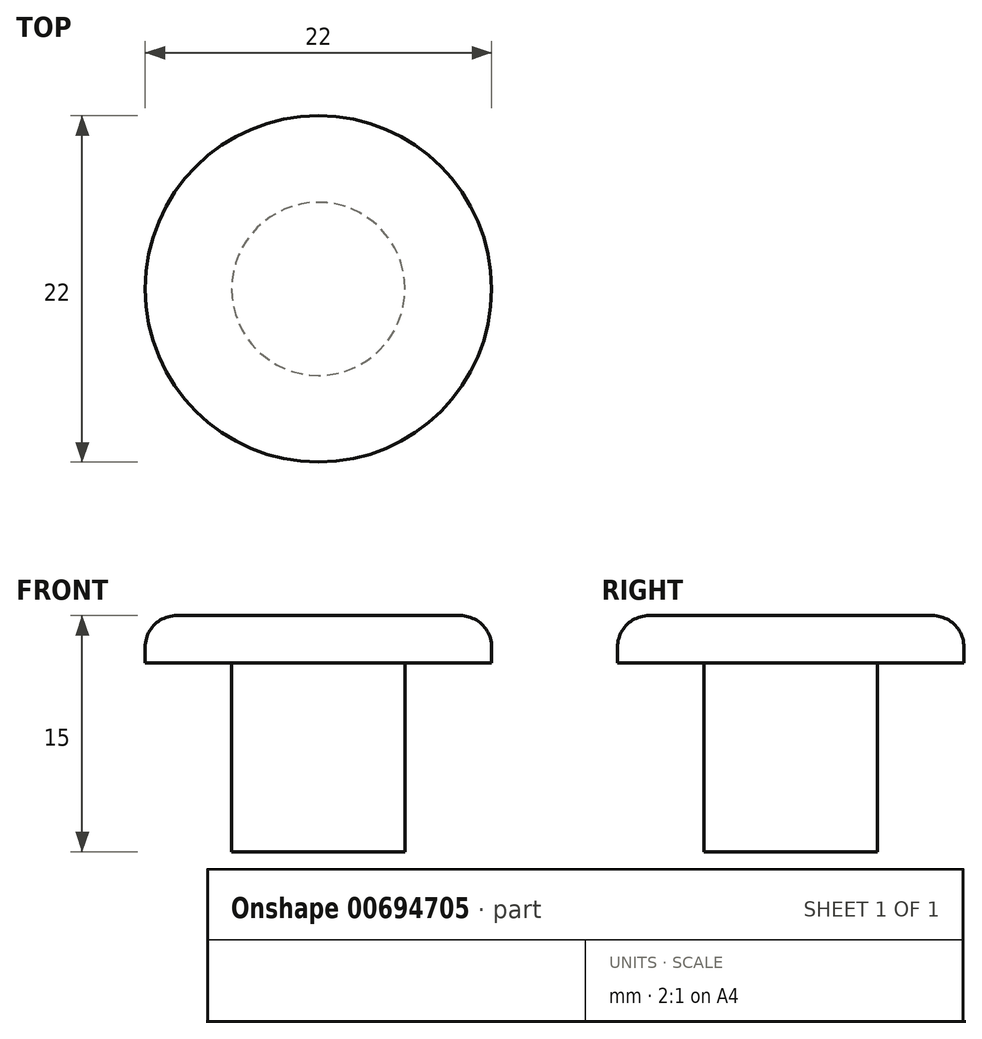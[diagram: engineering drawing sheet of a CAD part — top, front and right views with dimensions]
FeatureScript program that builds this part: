
annotation { "Feature Type Name" : "Feature", "Feature Type Description" : "" }
export const myFeature = defineFeature(function(context is Context, id is Id, definition is map)
    precondition{}
    {
        {
            var Q0;
            Q0=qCreatedBy(makeId("Top.planeOp"),FACE);
            var sketch = newSketch(context, id + "F0", { "sketchPlane" : qUnion([Q0])});
            skCircle(sketch, "E0", {"center": v(0, 0) * mm, "radius": 5.5 * mm});
            skCircle(sketch, "E1", {"center": v(0, 0) * mm, "radius": 11 * mm});
            skSolve(sketch);
        }
        {
            var Q0;
            Q0=makeQuery(id+"F0.imprint","IMPRINT",FACE,{"disambiguationData":[TD([[makeQuery(id+"F0.imprint","IMPRINT",EDGE,{"derivedFrom":sQuery(id+"F0.wireOp",EDGE,"E0")}),-1.0]])]});
            var Q1;
            Q1=makeQuery(id+"F0.imprint","IMPRINT",FACE,{"disambiguationData":[TD([[makeQuery(id+"F0.imprint","IMPRINT",EDGE,{"derivedFrom":sQuery(id+"F0.wireOp",EDGE,"E0")}),1.0]])]});
            extrude(context, id + "F1", {"entities" : qUnion([Q0, Q1]), "depth" : 3 * mm, "offsetDistance" : 25 * mm});
        }
        {
            var Q0;
            Q0=makeQuery(id+"F0.imprint","IMPRINT",FACE,{"disambiguationData":[TD([[makeQuery(id+"F0.imprint","IMPRINT",EDGE,{"derivedFrom":sQuery(id+"F0.wireOp",EDGE,"E0")}),1.0]])]});
            extrude(context, id + "F2", {"entities" : qUnion([Q0]), "operationType" : NewBodyOperationType.ADD, "oppositeDirection" : true, "depth" : 12 * mm, "offsetDistance" : 25 * mm});
        }
        {
            var Q0;
            Q0=makeQuery(id+"F1.opExtrude","CAP_FACE",FACE,{"disambiguationData":[OSD([sQuery(id+"F0.wireOp",EDGE,"E1")])],"isStart":false});
            fillet(context, id + "F3", {"entities" : qUnion([Q0]), "radius" : 2 * mm, "tangentPropagation" : true, "allowEdgeOverflow" : false});
        }
    });
